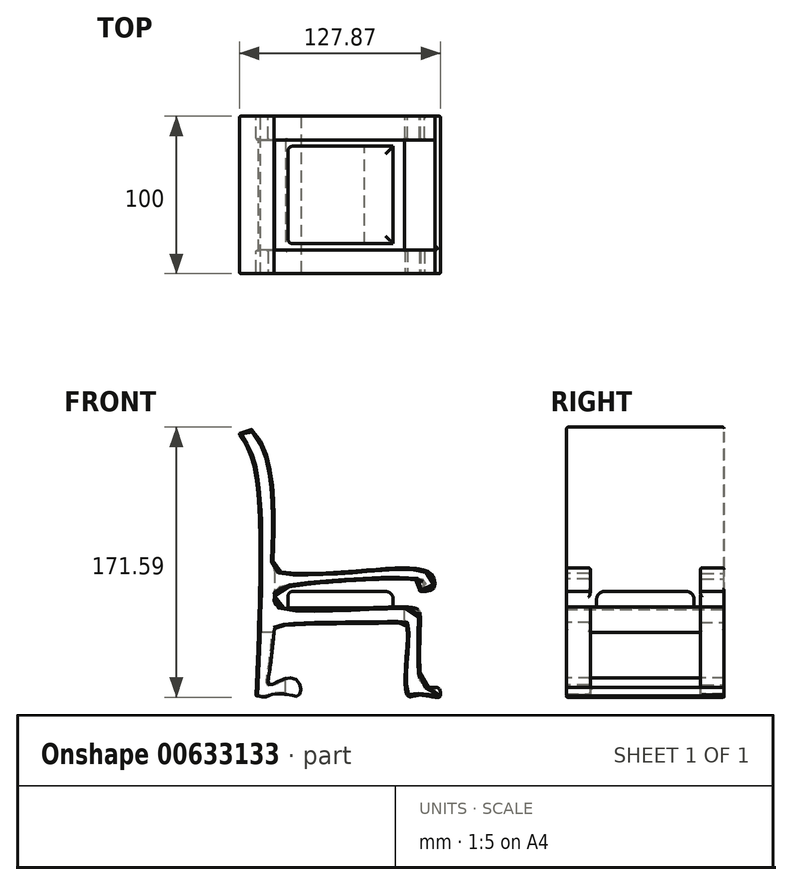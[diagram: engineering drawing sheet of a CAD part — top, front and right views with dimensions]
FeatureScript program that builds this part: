
annotation { "Feature Type Name" : "Feature", "Feature Type Description" : "" }
export const myFeature = defineFeature(function(context is Context, id is Id, definition is map)
    precondition{}
    {
        {
            var Q0;
            Q0=qCreatedBy(makeId("Front.planeOp"),FACE);
            var sketch = newSketch(context, id + "F0", { "sketchPlane" : qUnion([Q0])});
            skFitSpline(sketch, "E0", {"points": [v(-64.46, 90.51) * mm, v(-54.74, 69.18) * mm, v(-53.66, -75.57) * mm], "startDerivative": vector(38.52, -55.88) * mm, "endDerivative": vector(-10.02, -248.87) * mm});
            skFitSpline(sketch, "E1", {"points": [v(-64.46, 90.51) * mm, v(-61.76, 94.56) * mm, v(-56.9, 93.75) * mm, v(-45.01, 69.18) * mm, v(-42.85, 10.85) * mm, v(-40.96, 4.1) * mm, v(9, 3.55) * mm, v(54.9, 3.55) * mm, v(59.77, -2.93) * mm, v(58.14, -8.06) * mm, v(50.04, -8.87) * mm, v(52.2, -5.63) * mm, v(52.47, -2.93) * mm, v(-38.26, -7.52) * mm, v(-41.23, -10.49) * mm, v(-40.96, -18.05) * mm, v(45.72, -19.67) * mm, v(50.58, -25.34) * mm, v(50.31, -58.83) * mm, v(55.17, -70.17) * mm, v(61.93, -70.7) * mm, v(63.55, -75.84) * mm], "startDerivative": vector(85.5, 195.31) * mm, "endDerivative": vector(14.9, -244.42) * mm});
            skFitSpline(sketch, "E2", {"points": [v(-42.04, -33.24) * mm, v(-45.33, -61.02) * mm, v(-45.49, -68.57) * mm, v(-39.15, -66.4) * mm, v(-29.83, -64.55) * mm, v(-25.18, -70.9) * mm, v(-27.42, -75.95) * mm, v(-31.52, -75.31) * mm, v(-43.72, -74.67) * mm, v(-45.4, -75.57) * mm, v(-48.86, -76.43) * mm, v(-53.66, -75.57) * mm], "startDerivative": vector(-17.85, -172.98) * mm, "endDerivative": vector(-65.14, 18.3) * mm});
            skFitSpline(sketch, "E3", {"points": [v(-42.04, -33.24) * mm, v(-38.43, -31.53) * mm, v(36.88, -29.29) * mm, v(42.01, -30.4) * mm, v(41.05, -59.8) * mm, v(43.14, -76.01) * mm, v(48.76, -75.37) * mm, v(58.08, -76.24) * mm, v(62.37, -76.53) * mm, v(63.55, -75.84) * mm], "startDerivative": vector(23.8, 28.77) * mm, "endDerivative": vector(26.39, 22.04) * mm});
            skSolve(sketch);
        }
        {
            var Q0;
            Q0=makeQuery(id+"F0.imprint","IMPRINT",FACE,{"disambiguationData":[TD([[makeQuery(id+"F0.imprint","IMPRINT",EDGE,{"derivedFrom":sQuery(id+"F0.wireOp",EDGE,"E0")}),1.0]])]});
            extrude(context, id + "F1", {"entities" : qUnion([Q0]), "depth" : 50 * mm, "offsetDistance" : 25 * mm, "hasSecondDirection" : true, "secondDirectionOppositeDirection" : true, "secondDirectionDepth" : 50 * mm});
        }
        {
            var Q0;
            Q0=qCreatedBy(makeId("Right.planeOp"),FACE);
            var sketch = newSketch(context, id + "F2", { "sketchPlane" : qUnion([Q0])});
            skLineSegment(sketch, "E4.bottom", {"start": v(-35, -79.75) * mm, "end": v(35, -79.75) * mm});
            skLineSegment(sketch, "E4.top", {"start": v(-35, 79.75) * mm, "end": v(35, 79.75) * mm});
            skLineSegment(sketch, "E4.left", {"start": v(-35, -79.75) * mm, "end": v(-35, 79.75) * mm});
            skLineSegment(sketch, "E4.right", {"start": v(35, -79.75) * mm, "end": v(35, 79.75) * mm});
            skPoint(sketch, "E4.middle", {"position": v(0, 0) * mm});
            skSolve(sketch);
        }
        {
            var Q0;
            Q0=makeQuery(id+"F2.imprint","IMPRINT",FACE,{"disambiguationData":[TD([[makeQuery(id+"F2.imprint","IMPRINT",EDGE,{"derivedFrom":sQuery(id+"F2.wireOp",EDGE,"E4.bottom")}),1.0]])]});
            extrude(context, id + "F3", {"entities" : qUnion([Q0]), "operationType" : NewBodyOperationType.REMOVE, "depth" : 60 * mm, "offsetDistance" : 25 * mm, "hasSecondDirection" : true, "secondDirectionOppositeDirection" : false, "secondDirectionDepth" : 40.5 * mm});
        }
        {
            var Q0;
            Q0=qCreatedBy(makeId("Right.planeOp"),FACE);
            var sketch = newSketch(context, id + "F4", { "sketchPlane" : qUnion([Q0])});
            skLineSegment(sketch, "E5.bottom", {"start": v(-35, 16.58) * mm, "end": v(35, 16.58) * mm});
            skLineSegment(sketch, "E5.top", {"start": v(-35, -16.58) * mm, "end": v(35, -16.58) * mm});
            skLineSegment(sketch, "E5.left", {"start": v(-35, 16.58) * mm, "end": v(-35, -16.58) * mm});
            skLineSegment(sketch, "E5.right", {"start": v(35, 16.58) * mm, "end": v(35, -16.58) * mm});
            skPoint(sketch, "E5.middle", {"position": v(0, 0) * mm});
            skSolve(sketch);
        }
        {
            var Q0;
            Q0=makeQuery(id+"F4.imprint","IMPRINT",FACE,{"disambiguationData":[TD([[makeQuery(id+"F4.imprint","IMPRINT",EDGE,{"derivedFrom":sQuery(id+"F4.wireOp",EDGE,"E5.bottom")}),-1.0]])]});
            extrude(context, id + "F5", {"entities" : qUnion([Q0]), "operationType" : NewBodyOperationType.REMOVE, "oppositeDirection" : true, "depth" : 42 * mm, "offsetDistance" : 25 * mm, "hasSecondDirection" : true, "secondDirectionOppositeDirection" : false, "secondDirectionDepth" : 54.1 * mm});
        }
        {
            var Q0;
            Q0=qCreatedBy(makeId("Right.planeOp"),FACE);
            cPlane(context, id + "F6", {"entities" : qUnion([Q0]), "cplaneType" : CPlaneType.OFFSET, "offset" : 80 * mm, "oppositeDirection" : true, "width" : 150 * mm, "height" : 150 * mm});
        }
        {
            var Q0;
            Q0=qCreatedBy(id+"F6.planeOp",FACE);
            var sketch = newSketch(context, id + "F7", { "sketchPlane" : qUnion([Q0])});
            skLineSegment(sketch, "E6.bottom", {"start": v(35, -135.54) * mm, "end": v(-35, -135.54) * mm});
            skLineSegment(sketch, "E6.top", {"start": v(35, -35.54) * mm, "end": v(-35, -35.54) * mm});
            skLineSegment(sketch, "E6.left", {"start": v(35, -135.54) * mm, "end": v(35, -35.54) * mm});
            skLineSegment(sketch, "E6.right", {"start": v(-35, -135.54) * mm, "end": v(-35, -35.54) * mm});
            skPoint(sketch, "E6.middle", {"position": v(0, -85.54) * mm});
            skSolve(sketch);
        }
        {
            var Q0;
            Q0=makeQuery(id+"F7.imprint","IMPRINT",FACE,{"disambiguationData":[TD([[makeQuery(id+"F7.imprint","IMPRINT",EDGE,{"derivedFrom":sQuery(id+"F7.wireOp",EDGE,"E6.bottom")}),-1.0]])]});
            extrude(context, id + "F8", {"entities" : qUnion([Q0]), "operationType" : NewBodyOperationType.REMOVE, "depth" : 45 * mm, "offsetDistance" : 25 * mm});
        }
        {
            var Q0;
            Q0=makeQuery(id+"F5.boolean.opBoolean","INTERSECT",EDGE,{"disambiguationData":[OD(1.0)],"derivedFrom":[makeQuery(id+"F1.opExtrude","SWEPT_FACE",FACE,{"disambiguationData":[OSD([sQuery(id+"F0.wireOp",EDGE,"E1")])]}),makeQuery(id+"F5.opExtrude","CAP_FACE",FACE,{"disambiguationData":[OSD([sQuery(id+"F4.wireOp",EDGE,"E5.bottom"),sQuery(id+"F4.wireOp",EDGE,"E5.top"),sQuery(id+"F4.wireOp",EDGE,"E5.left"),sQuery(id+"F4.wireOp",EDGE,"E5.right")])],"isStart":false})]});
            var Q1;
            Q1=makeQuery(id+"F5.boolean.opBoolean","INTERSECT",EDGE,{"disambiguationData":[OD(0.0)],"derivedFrom":[makeQuery(id+"F1.opExtrude","SWEPT_FACE",FACE,{"disambiguationData":[OSD([sQuery(id+"F0.wireOp",EDGE,"E1")])]}),makeQuery(id+"F5.opExtrude","CAP_FACE",FACE,{"disambiguationData":[OSD([sQuery(id+"F4.wireOp",EDGE,"E5.bottom"),sQuery(id+"F4.wireOp",EDGE,"E5.top"),sQuery(id+"F4.wireOp",EDGE,"E5.left"),sQuery(id+"F4.wireOp",EDGE,"E5.right")])],"isStart":false})]});
            fillet(context, id + "F9", {"entities" : qUnion([Q0, Q1]), "radius" : 2 * mm, "tangentPropagation" : true, "allowEdgeOverflow" : false});
        }
        {
            var Q0;
            Q0=makeQuery(id+"F5.boolean.opBoolean","INTERSECT",EDGE,{"derivedFrom":[makeQuery(id+"F1.opExtrude","SWEPT_FACE",FACE,{"disambiguationData":[OSD([sQuery(id+"F0.wireOp",EDGE,"E1")])]}),makeQuery(id+"F5.opExtrude","SWEPT_FACE",FACE,{"disambiguationData":[OSD([sQuery(id+"F4.wireOp",EDGE,"E5.left")])]})]});
            var Q1;
            Q1=makeQuery(id+"F5.boolean.opBoolean","INTERSECT",EDGE,{"derivedFrom":[makeQuery(id+"F1.opExtrude","SWEPT_FACE",FACE,{"disambiguationData":[OSD([sQuery(id+"F0.wireOp",EDGE,"E1")])]}),makeQuery(id+"F5.opExtrude","SWEPT_FACE",FACE,{"disambiguationData":[OSD([sQuery(id+"F4.wireOp",EDGE,"E5.right")])]})]});
            var Q2;
            Q2=makeQuery(id+"F1.opExtrude","CAP_EDGE",EDGE,{"disambiguationData":[OSD([sQuery(id+"F0.wireOp",EDGE,"E1")])],"isStart":false});
            var Q3;
            Q3=makeQuery(id+"F1.opExtrude","CAP_EDGE",EDGE,{"disambiguationData":[OSD([sQuery(id+"F0.wireOp",EDGE,"E1")])],"isStart":true});
            var Q4;
            Q4=makeQuery(id+"F3.boolean.opBoolean","INTERSECT",EDGE,{"disambiguationData":[OD(0.0)],"derivedFrom":[makeQuery(id+"F1.opExtrude","SWEPT_FACE",FACE,{"disambiguationData":[OSD([sQuery(id+"F0.wireOp",EDGE,"E1")])]}),makeQuery(id+"F3.opExtrude","CAP_FACE",FACE,{"disambiguationData":[OSD([sQuery(id+"F2.wireOp",EDGE,"E4.bottom"),sQuery(id+"F2.wireOp",EDGE,"E4.top"),sQuery(id+"F2.wireOp",EDGE,"E4.left"),sQuery(id+"F2.wireOp",EDGE,"E4.right")])],"isStart":true})]});
            var Q5;
            Q5=makeQuery(id+"F3.boolean.opBoolean","INTERSECT",EDGE,{"disambiguationData":[OD(0.0)],"derivedFrom":[makeQuery(id+"F1.opExtrude","SWEPT_FACE",FACE,{"disambiguationData":[OSD([sQuery(id+"F0.wireOp",EDGE,"E1")])]}),makeQuery(id+"F3.opExtrude","SWEPT_FACE",FACE,{"disambiguationData":[OSD([sQuery(id+"F2.wireOp",EDGE,"E4.left")])]})]});
            var Q6;
            Q6=makeQuery(id+"F3.boolean.opBoolean","INTERSECT",EDGE,{"derivedFrom":[makeQuery(id+"F1.opExtrude","SWEPT_FACE",FACE,{"disambiguationData":[OSD([sQuery(id+"F0.wireOp",EDGE,"E3")])]}),makeQuery(id+"F3.opExtrude","CAP_FACE",FACE,{"disambiguationData":[OSD([sQuery(id+"F2.wireOp",EDGE,"E4.bottom"),sQuery(id+"F2.wireOp",EDGE,"E4.top"),sQuery(id+"F2.wireOp",EDGE,"E4.left"),sQuery(id+"F2.wireOp",EDGE,"E4.right")])],"isStart":true})]});
            var Q7;
            {var subQ0=sQuery(id+"F2.wireOp",EDGE,"E4.left");Q7=makeQuery(id+"F3.boolean.opBoolean","COPY",EDGE,{"disambiguationData":[TD([makeQuery(id+"F1.opExtrude","SWEPT_FACE",FACE,{"disambiguationData":[OSD([sQuery(id+"F0.wireOp",EDGE,"E1")])]}),makeQuery(id+"F1.opExtrude","SWEPT_FACE",FACE,{"disambiguationData":[OSD([sQuery(id+"F0.wireOp",EDGE,"E3")])]}),makeQuery(id+"F3.opExtrude","CAP_FACE",FACE,{"disambiguationData":[OSD([sQuery(id+"F2.wireOp",EDGE,"E4.bottom"),sQuery(id+"F2.wireOp",EDGE,"E4.top"),subQ0,sQuery(id+"F2.wireOp",EDGE,"E4.right")])],"isStart":true}),makeQuery(id+"F3.opExtrude","SWEPT_FACE",FACE,{"disambiguationData":[OSD([subQ0])]})])],"derivedFrom":makeQuery(id+"F3.opExtrude","CAP_EDGE",EDGE,{"disambiguationData":[OSD([subQ0])],"isStart":true})});}
            var Q8;
            Q8=makeQuery(id+"F3.boolean.opBoolean","INTERSECT",EDGE,{"disambiguationData":[OD(0.0)],"derivedFrom":[makeQuery(id+"F1.opExtrude","SWEPT_FACE",FACE,{"disambiguationData":[OSD([sQuery(id+"F0.wireOp",EDGE,"E1")])]}),makeQuery(id+"F3.opExtrude","SWEPT_FACE",FACE,{"disambiguationData":[OSD([sQuery(id+"F2.wireOp",EDGE,"E4.right")])]})]});
            var Q9;
            {var subQ0=sQuery(id+"F2.wireOp",EDGE,"E4.right");Q9=makeQuery(id+"F3.boolean.opBoolean","COPY",EDGE,{"disambiguationData":[TD([makeQuery(id+"F1.opExtrude","SWEPT_FACE",FACE,{"disambiguationData":[OSD([sQuery(id+"F0.wireOp",EDGE,"E1")])]}),makeQuery(id+"F1.opExtrude","SWEPT_FACE",FACE,{"disambiguationData":[OSD([sQuery(id+"F0.wireOp",EDGE,"E3")])]}),makeQuery(id+"F3.opExtrude","CAP_FACE",FACE,{"disambiguationData":[OSD([sQuery(id+"F2.wireOp",EDGE,"E4.bottom"),sQuery(id+"F2.wireOp",EDGE,"E4.top"),sQuery(id+"F2.wireOp",EDGE,"E4.left"),subQ0])],"isStart":true}),makeQuery(id+"F3.opExtrude","SWEPT_FACE",FACE,{"disambiguationData":[OSD([subQ0])]})])],"derivedFrom":makeQuery(id+"F3.opExtrude","CAP_EDGE",EDGE,{"disambiguationData":[OSD([subQ0])],"isStart":true})});}
            var Q10;
            Q10=makeQuery(id+"F1.opExtrude","CAP_EDGE",EDGE,{"disambiguationData":[OSD([sQuery(id+"F0.wireOp",EDGE,"E3")])],"isStart":true});
            var Q11;
            Q11=makeQuery(id+"F3.boolean.opBoolean","INTERSECT",EDGE,{"derivedFrom":[makeQuery(id+"F1.opExtrude","SWEPT_FACE",FACE,{"disambiguationData":[OSD([sQuery(id+"F0.wireOp",EDGE,"E3")])]}),makeQuery(id+"F3.opExtrude","SWEPT_FACE",FACE,{"disambiguationData":[OSD([sQuery(id+"F2.wireOp",EDGE,"E4.right")])]})]});
            var Q12;
            Q12=makeQuery(id+"F3.boolean.opBoolean","COPY",EDGE,{"derivedFrom":makeQuery(id+"F3.opExtrude","CAP_EDGE",EDGE,{"disambiguationData":[OSD([sQuery(id+"F2.wireOp",EDGE,"E4.left")])],"isStart":false})});
            var Q13;
            Q13=makeQuery(id+"F1.opExtrude","CAP_EDGE",EDGE,{"disambiguationData":[OSD([sQuery(id+"F0.wireOp",EDGE,"E3")])],"isStart":false});
            var Q14;
            Q14=makeQuery(id+"F1.opExtrude","SWEPT_EDGE",EDGE,{"disambiguationData":[OSD([sQuery(id+"F0.wireOp",EDGE,"E2"),sQuery(id+"F0.wireOp",EDGE,"E3")])]});
            var Q15;
            Q15=makeQuery(id+"F8.boolean.opBoolean","INTERSECT",EDGE,{"derivedFrom":[makeQuery(id+"F1.opExtrude","SWEPT_FACE",FACE,{"disambiguationData":[OSD([sQuery(id+"F0.wireOp",EDGE,"E2")])]}),makeQuery(id+"F8.opExtrude","SWEPT_FACE",FACE,{"disambiguationData":[OSD([sQuery(id+"F7.wireOp",EDGE,"E6.top")])]})]});
            var Q16;
            Q16=makeQuery(id+"F8.boolean.opBoolean","INTERSECT",EDGE,{"disambiguationData":[OD(0.0)],"derivedFrom":[makeQuery(id+"F1.opExtrude","SWEPT_FACE",FACE,{"disambiguationData":[OSD([sQuery(id+"F0.wireOp",EDGE,"E2")])]}),makeQuery(id+"F8.opExtrude","SWEPT_FACE",FACE,{"disambiguationData":[OSD([sQuery(id+"F7.wireOp",EDGE,"E6.right")])]})]});
            var Q17;
            Q17=makeQuery(id+"F1.opExtrude","CAP_EDGE",EDGE,{"disambiguationData":[OSD([sQuery(id+"F0.wireOp",EDGE,"E0")])],"isStart":false});
            var Q18;
            Q18=makeQuery(id+"F8.boolean.opBoolean","INTERSECT",EDGE,{"disambiguationData":[OD(1.0)],"derivedFrom":[makeQuery(id+"F1.opExtrude","SWEPT_FACE",FACE,{"disambiguationData":[OSD([sQuery(id+"F0.wireOp",EDGE,"E2")])]}),makeQuery(id+"F8.opExtrude","CAP_FACE",FACE,{"disambiguationData":[OSD([sQuery(id+"F7.wireOp",EDGE,"E6.bottom"),sQuery(id+"F7.wireOp",EDGE,"E6.top"),sQuery(id+"F7.wireOp",EDGE,"E6.left"),sQuery(id+"F7.wireOp",EDGE,"E6.right")])],"isStart":false})]});
            var Q19;
            Q19=makeQuery(id+"F8.boolean.opBoolean","INTERSECT",EDGE,{"disambiguationData":[OD(1.0)],"derivedFrom":[makeQuery(id+"F1.opExtrude","SWEPT_FACE",FACE,{"disambiguationData":[OSD([sQuery(id+"F0.wireOp",EDGE,"E2")])]}),makeQuery(id+"F8.opExtrude","SWEPT_FACE",FACE,{"disambiguationData":[OSD([sQuery(id+"F7.wireOp",EDGE,"E6.left")])]})]});
            var Q20;
            Q20=makeQuery(id+"F8.boolean.opBoolean","INTERSECT",EDGE,{"disambiguationData":[OD(0.0)],"derivedFrom":[makeQuery(id+"F1.opExtrude","SWEPT_FACE",FACE,{"disambiguationData":[OSD([sQuery(id+"F0.wireOp",EDGE,"E2")])]}),makeQuery(id+"F8.opExtrude","SWEPT_FACE",FACE,{"disambiguationData":[OSD([sQuery(id+"F7.wireOp",EDGE,"E6.left")])]})]});
            var Q21;
            Q21=makeQuery(id+"F8.boolean.opBoolean","INTERSECT",EDGE,{"disambiguationData":[OD(0.0)],"derivedFrom":[makeQuery(id+"F1.opExtrude","SWEPT_FACE",FACE,{"disambiguationData":[OSD([sQuery(id+"F0.wireOp",EDGE,"E2")])]}),makeQuery(id+"F8.opExtrude","CAP_FACE",FACE,{"disambiguationData":[OSD([sQuery(id+"F7.wireOp",EDGE,"E6.bottom"),sQuery(id+"F7.wireOp",EDGE,"E6.top"),sQuery(id+"F7.wireOp",EDGE,"E6.left"),sQuery(id+"F7.wireOp",EDGE,"E6.right")])],"isStart":false})]});
            var Q22;
            Q22=makeQuery(id+"F8.boolean.opBoolean","INTERSECT",EDGE,{"derivedFrom":[makeQuery(id+"F1.opExtrude","SWEPT_FACE",FACE,{"disambiguationData":[OSD([sQuery(id+"F0.wireOp",EDGE,"E0")])]}),makeQuery(id+"F8.opExtrude","SWEPT_FACE",FACE,{"disambiguationData":[OSD([sQuery(id+"F7.wireOp",EDGE,"E6.right")])]})]});
            var Q23;
            Q23=makeQuery(id+"F8.boolean.opBoolean","INTERSECT",EDGE,{"disambiguationData":[OD(1.0)],"derivedFrom":[makeQuery(id+"F1.opExtrude","SWEPT_FACE",FACE,{"disambiguationData":[OSD([sQuery(id+"F0.wireOp",EDGE,"E2")])]}),makeQuery(id+"F8.opExtrude","SWEPT_FACE",FACE,{"disambiguationData":[OSD([sQuery(id+"F7.wireOp",EDGE,"E6.right")])]})]});
            var Q24;
            Q24=makeQuery(id+"F8.boolean.opBoolean","INTERSECT",EDGE,{"derivedFrom":[makeQuery(id+"F1.opExtrude","SWEPT_FACE",FACE,{"disambiguationData":[OSD([sQuery(id+"F0.wireOp",EDGE,"E0")])]}),makeQuery(id+"F8.opExtrude","SWEPT_FACE",FACE,{"disambiguationData":[OSD([sQuery(id+"F7.wireOp",EDGE,"E6.top")])]})]});
            var Q25;
            Q25=makeQuery(id+"F8.boolean.opBoolean","INTERSECT",EDGE,{"derivedFrom":[makeQuery(id+"F1.opExtrude","SWEPT_FACE",FACE,{"disambiguationData":[OSD([sQuery(id+"F0.wireOp",EDGE,"E0")])]}),makeQuery(id+"F8.opExtrude","SWEPT_FACE",FACE,{"disambiguationData":[OSD([sQuery(id+"F7.wireOp",EDGE,"E6.left")])]})]});
            var Q26;
            Q26=makeQuery(id+"F1.opExtrude","CAP_EDGE",EDGE,{"disambiguationData":[OSD([sQuery(id+"F0.wireOp",EDGE,"E0")])],"isStart":true});
            var Q27;
            Q27=makeQuery(id+"F1.opExtrude","SWEPT_EDGE",EDGE,{"disambiguationData":[OSD([sQuery(id+"F0.wireOp",EDGE,"E0"),sQuery(id+"F0.wireOp",EDGE,"E1")])]});
            fillet(context, id + "F10", {"entities" : qUnion([Q0, Q1, Q2, Q3, Q4, Q5, Q6, Q7, Q8, Q9, Q10, Q11, Q12, Q13, Q14, Q15, Q16, Q17, Q18, Q19, Q20, Q21, Q22, Q23, Q24, Q25, Q26, Q27]), "radius" : 1 * mm, "tangentPropagation" : true, "allowEdgeOverflow" : false});
        }
        {
            var Q0;
            Q0=qCreatedBy(makeId("Top.planeOp"),FACE);
            var sketch = newSketch(context, id + "F11", { "sketchPlane" : qUnion([Q0])});
            skLineSegment(sketch, "E7.bottom", {"start": v(33.4, 30.97) * mm, "end": v(-33.4, 30.97) * mm});
            skLineSegment(sketch, "E7.top", {"start": v(33.4, -30.97) * mm, "end": v(-33.4, -30.97) * mm});
            skLineSegment(sketch, "E7.left", {"start": v(33.4, 30.97) * mm, "end": v(33.4, -30.97) * mm});
            skLineSegment(sketch, "E7.right", {"start": v(-33.4, 30.97) * mm, "end": v(-33.4, -30.97) * mm});
            skPoint(sketch, "E7.middle", {"position": v(0, 0) * mm});
            skSolve(sketch);
        }
        {
            var Q0;
            Q0 = qSketchRegion(id + "F11", true);
            extrude(context, id + "F12", {"entities" : qUnion([Q0]), "operationType" : NewBodyOperationType.ADD, "oppositeDirection" : true, "depth" : 20 * mm, "offsetDistance" : 25 * mm, "hasSecondDirection" : true, "secondDirectionOppositeDirection" : true, "secondDirectionDepth" : 9.4 * mm});
        }
        {
            var Q0;
            Q0=makeQuery(id+"F12.opExtrude","CAP_EDGE",EDGE,{"disambiguationData":[OSD([sQuery(id+"F11.wireOp",EDGE,"E7.left")])],"isStart":true});
            var Q1;
            Q1=makeQuery(id+"F12.opExtrude","CAP_EDGE",EDGE,{"disambiguationData":[OSD([sQuery(id+"F11.wireOp",EDGE,"E7.top")])],"isStart":true});
            var Q2;
            Q2=makeQuery(id+"F12.opExtrude","CAP_EDGE",EDGE,{"disambiguationData":[OSD([sQuery(id+"F11.wireOp",EDGE,"E7.bottom")])],"isStart":true});
            fillet(context, id + "F13", {"entities" : qUnion([Q0, Q1, Q2]), "radius" : 5 * mm, "tangentPropagation" : true, "allowEdgeOverflow" : false});
        }
        {
            var Q0;
            Q0=makeQuery(id+"F12.opExtrude","CAP_EDGE",EDGE,{"disambiguationData":[OSD([sQuery(id+"F11.wireOp",EDGE,"E7.right")])],"isStart":true});
            fillet(context, id + "F14", {"entities" : qUnion([Q0]), "radius" : 3 * mm, "tangentPropagation" : true, "allowEdgeOverflow" : false});
        }
    });
